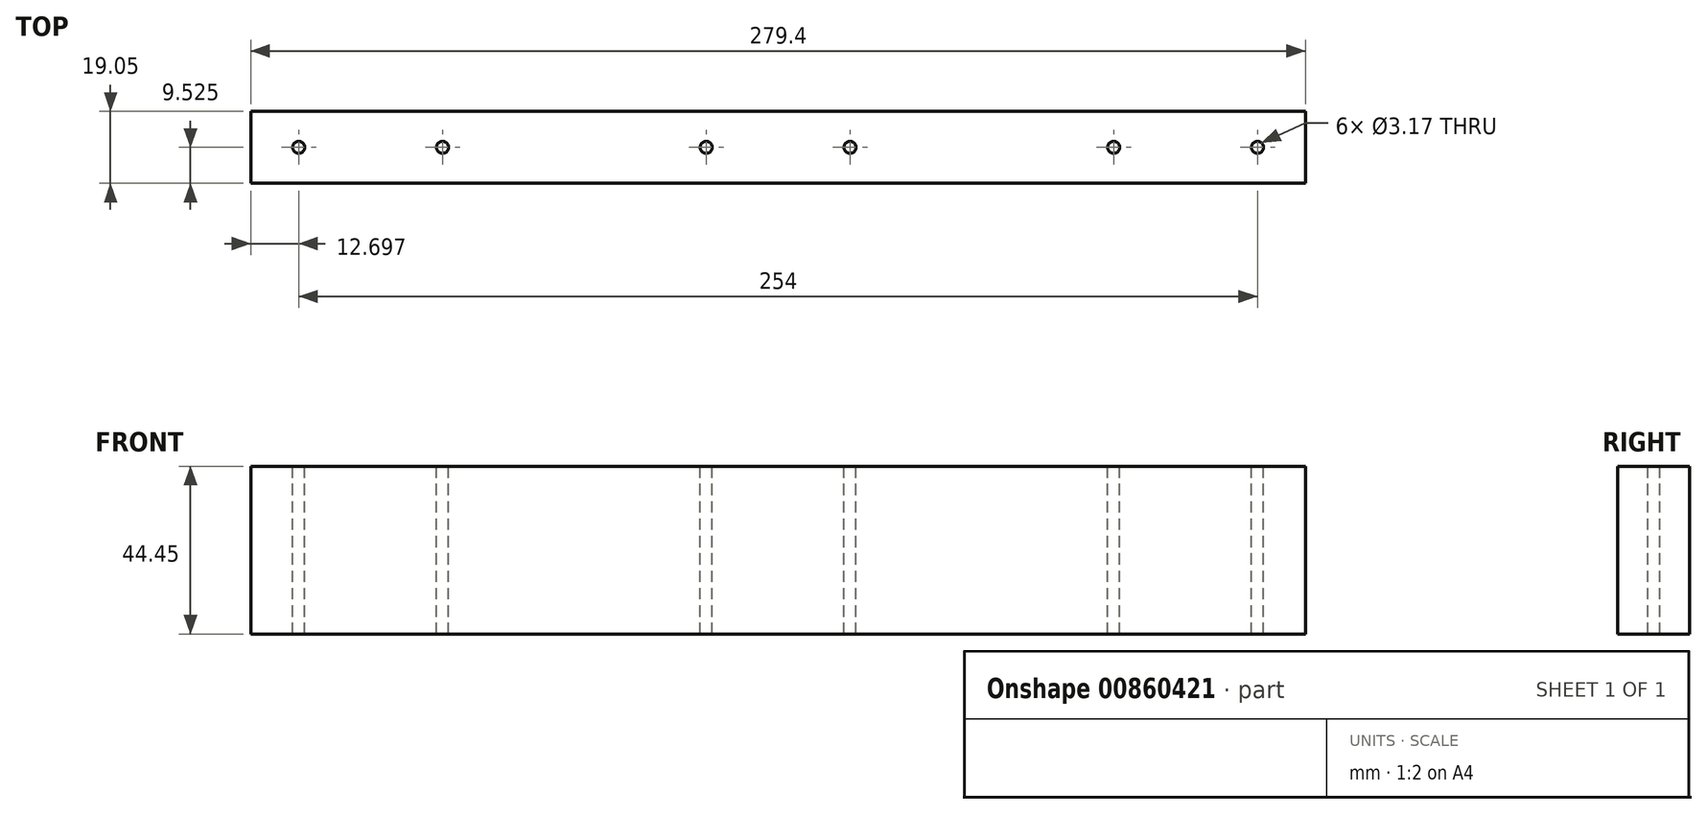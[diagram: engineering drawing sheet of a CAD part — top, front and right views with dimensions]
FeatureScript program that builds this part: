
annotation { "Feature Type Name" : "Feature", "Feature Type Description" : "" }
export const myFeature = defineFeature(function(context is Context, id is Id, definition is map)
    precondition{}
    {
        {
            var Q0;
            Q0=qCreatedBy(makeId("Front.planeOp"),FACE);
            var sketch = newSketch(context, id + "F0", { "sketchPlane" : qUnion([Q0])});
            skLineSegment(sketch, "E0.bottom", {"start": v(-216.73, 42.2) * mm, "end": v(62.67, 42.2) * mm});
            skLineSegment(sketch, "E0.top", {"start": v(-216.73, -2.24) * mm, "end": v(62.67, -2.24) * mm});
            skLineSegment(sketch, "E0.left", {"start": v(-216.73, 42.2) * mm, "end": v(-216.73, -2.24) * mm});
            skLineSegment(sketch, "E0.right", {"start": v(62.67, 42.2) * mm, "end": v(62.67, -2.24) * mm});
            skSolve(sketch);
        }
        {
            var Q0;
            Q0=makeQuery(id+"F0.imprint","IMPRINT",FACE,{"disambiguationData":[TD([[makeQuery(id+"F0.imprint","IMPRINT",EDGE,{"derivedFrom":sQuery(id+"F0.wireOp",EDGE,"E0.bottom")}),-1.0]])]});
            extrude(context, id + "F1", {"entities" : qUnion([Q0]), "depth" : 19.05 * mm, "offsetDistance" : 25.4 * mm});
        }
        {
            var Q0;
            Q0=makeQuery(id+"F1.opExtrude","SWEPT_FACE",FACE,{"disambiguationData":[OSD([sQuery(id+"F0.wireOp",EDGE,"E0.bottom")])]});
            var sketch = newSketch(context, id + "F2", { "sketchPlane" : qUnion([Q0])});
            skLineSegment(sketch, "E1", {"start": v(62.67, -9.53) * mm, "end": v(-216.73, -9.53) * mm, "construction": true});
            skPoint(sketch, "E2", {"position": v(-204.03, -9.53) * mm});
            skPoint(sketch, "E3", {"position": v(-96.08, -9.53) * mm});
            skPoint(sketch, "E4", {"position": v(11.87, -9.53) * mm});
            skPoint(sketch, "E5", {"position": v(-165.93, -9.53) * mm});
            skPoint(sketch, "E6", {"position": v(-57.98, -9.53) * mm});
            skPoint(sketch, "E7", {"position": v(49.97, -9.53) * mm});
            skSolve(sketch);
        }
        {
            var Q0;
            Q0=sQuery(id+"F2.wireOp",VERTEX,"E2");
            var Q1;
            Q1=sQuery(id+"F2.wireOp",VERTEX,"E5");
            var Q2;
            Q2=sQuery(id+"F2.wireOp",VERTEX,"E3");
            var Q3;
            Q3=sQuery(id+"F2.wireOp",VERTEX,"E6");
            var Q4;
            Q4=sQuery(id+"F2.wireOp",VERTEX,"E4");
            var Q5;
            Q5=sQuery(id+"F2.wireOp",VERTEX,"E7");
            var Q6;
            Q6=makeQuery(id+"F1.opExtrude","SWEPT_BODY",BODY,{"disambiguationData":[OSD([sQuery(id+"F0.wireOp",EDGE,"E0.bottom"),sQuery(id+"F0.wireOp",EDGE,"E0.top"),sQuery(id+"F0.wireOp",EDGE,"E0.left"),sQuery(id+"F0.wireOp",EDGE,"E0.right")])]});
            hole(context, id + "F3", {"style" : HoleStyle.SIMPLE, "endStyle" : HoleEndStyle.THROUGH, "holeDiameter" : 3.17 * mm, "majorDiameter" : 6.35 * mm, "isTappedThrough" : true, "tappedDepth" : 12.7 * mm, "tapClearance" : 3, "locations" : qUnion([Q0, Q1, Q2, Q3, Q4, Q5]), "scope" : qUnion([Q6])});
        }
    });
